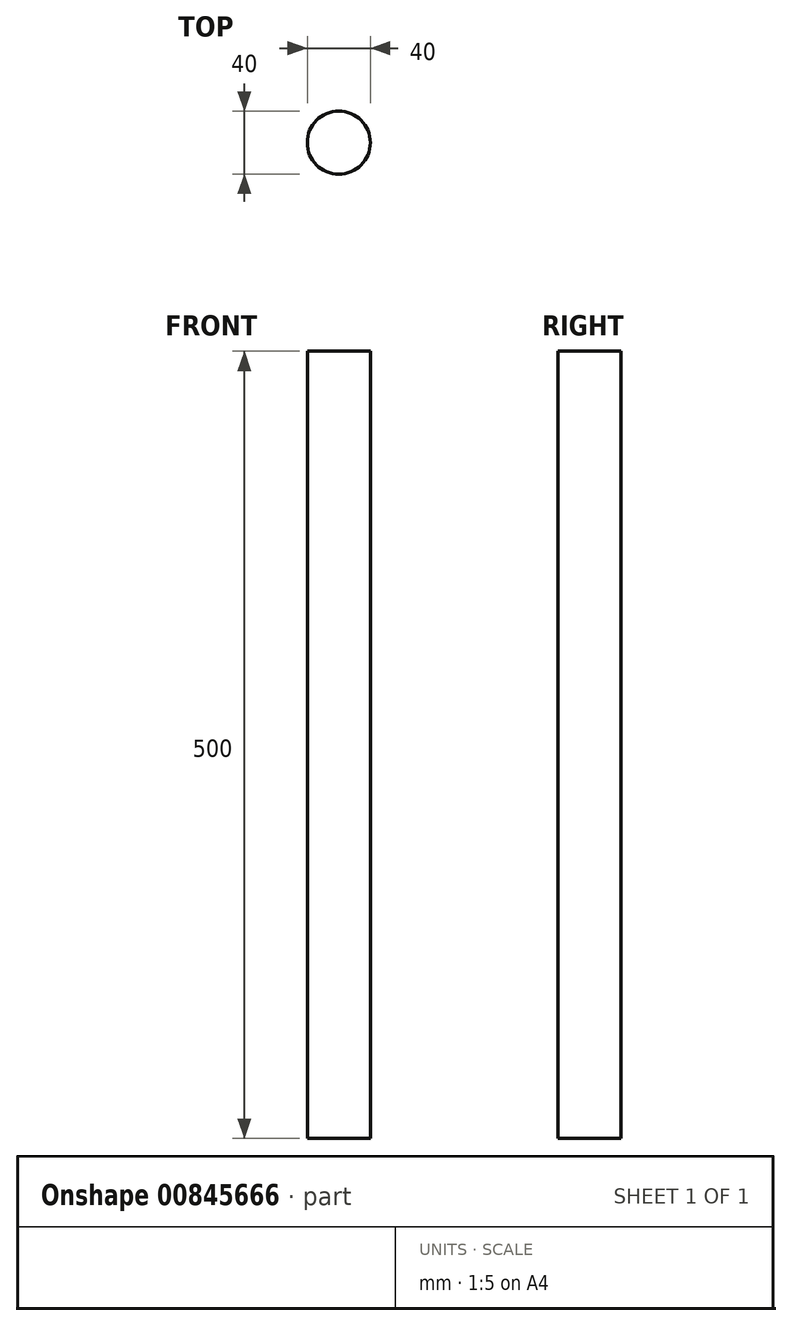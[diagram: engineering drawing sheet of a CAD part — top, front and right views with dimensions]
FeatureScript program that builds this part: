
annotation { "Feature Type Name" : "Feature", "Feature Type Description" : "" }
export const myFeature = defineFeature(function(context is Context, id is Id, definition is map)
    precondition{}
    {
        {
            var Q0;
            Q0=qCreatedBy(makeId("Top.planeOp"),FACE);
            var sketch = newSketch(context, id + "F0", { "sketchPlane" : qUnion([Q0])});
            skCircle(sketch, "E0", {"center": v(0, 0) * mm, "radius": 20 * mm});
            skSolve(sketch);
        }
        {
            var Q0;
            Q0=sQuery(id+"F0.wireOp",EDGE,"E0");
            extrude(context, id + "F1", {"bodyType" : ToolBodyType.SURFACE, "surfaceEntities" : qUnion([Q0]), "depth" : 500 * mm, "offsetDistance" : 25.4 * mm});
        }
    });
